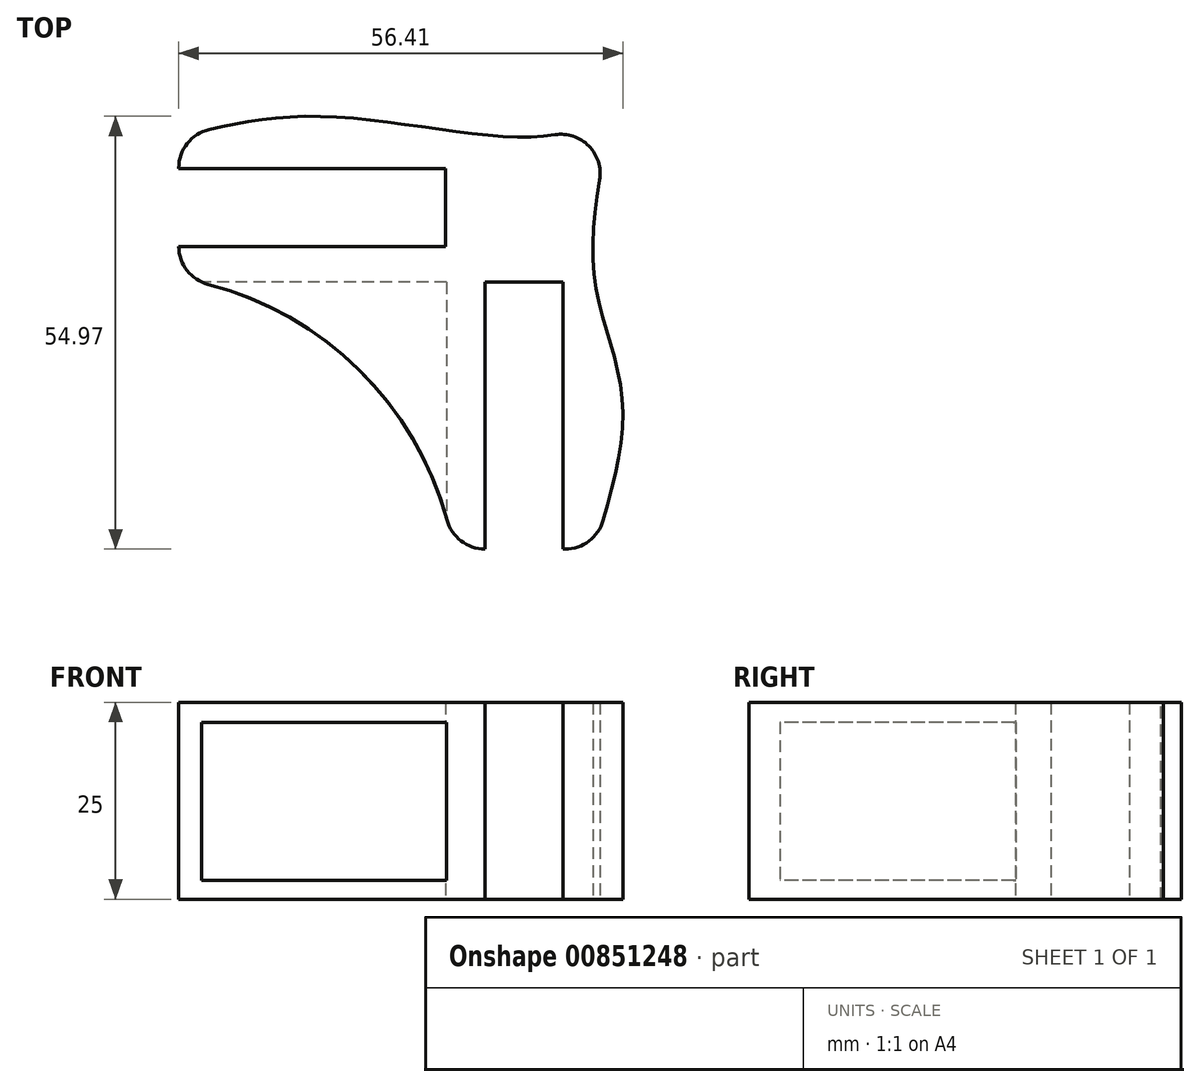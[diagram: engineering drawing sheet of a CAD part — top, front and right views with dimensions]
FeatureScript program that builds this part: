
annotation { "Feature Type Name" : "Feature", "Feature Type Description" : "" }
export const myFeature = defineFeature(function(context is Context, id is Id, definition is map)
    precondition{}
    {
        {
            var Q0;
            Q0=qCreatedBy(makeId("Top.planeOp"),FACE);
            var sketch = newSketch(context, id + "F0", { "sketchPlane" : qUnion([Q0])});
            skLineSegment(sketch, "E0.bottom", {"start": v(46.13, 46.63) * mm, "end": v(-43.87, 46.63) * mm, "construction": true});
            skLineSegment(sketch, "E0.top", {"start": v(46.13, -43.37) * mm, "end": v(-43.87, -43.37) * mm, "construction": true});
            skLineSegment(sketch, "E0.left", {"start": v(46.13, 46.63) * mm, "end": v(46.13, -43.37) * mm, "construction": true});
            skLineSegment(sketch, "E1", {"start": v(4.96, -9.48) * mm, "end": v(4.96, -43.37) * mm});
            skLineSegment(sketch, "E2", {"start": v(-4.96, -9.48) * mm, "end": v(-4.96, -43.37) * mm});
            skLineSegment(sketch, "E3", {"start": v(-10, 4.96) * mm, "end": v(-43.87, 4.96) * mm});
            skLineSegment(sketch, "E4", {"start": v(-10, -4.96) * mm, "end": v(-43.87, -4.96) * mm});
            skLineSegment(sketch, "E5", {"start": v(-10, -4.96) * mm, "end": v(-10, 4.96) * mm});
            skLineSegment(sketch, "E6", {"start": v(-4.96, -9.48) * mm, "end": v(4.96, -9.48) * mm});
            skLineSegment(sketch, "E7", {"start": v(-43.87, -4.96) * mm, "end": v(-43.87, -8.96) * mm});
            skLineSegment(sketch, "E8", {"start": v(-4.96, -43.37) * mm, "end": v(-4.97, -43.37) * mm});
            skLineSegment(sketch, "E9", {"start": v(-43.87, 4.96) * mm, "end": v(-43.87, 8.96) * mm});
            skLineSegment(sketch, "E10", {"start": v(4.96, -43.37) * mm, "end": v(8.96, -43.37) * mm});
            skFitSpline(sketch, "E11", {"points": [v(-43.87, 8.96) * mm, v(-25.72, 11.58) * mm, v(0, 8.96) * mm, v(11.1, 11.21) * mm], "startDerivative": vector(49.68, 12.5) * mm, "endDerivative": vector(36.5, 12.65) * mm});
            skFitSpline(sketch, "E12", {"points": [v(8.96, -43.37) * mm, v(12.48, -24.43) * mm, v(8.96, -8.93) * mm, v(11.1, 11.21) * mm], "startDerivative": vector(17.47, 57.6) * mm, "endDerivative": vector(12.47, 60.14) * mm});
            skArc(sketch, "E13", {"start": v(-9.8, -39.69) * mm, "mid": v(-22.32, -19.33) * mm, "end": v(-43.87, -8.96) * mm});
            skLineSegment(sketch, "E14.bottom", {"start": v(24.76, 22.31) * mm, "end": v(24.23, 22.31) * mm});
            skLineSegment(sketch, "E14.top", {"start": v(24.76, -47.4) * mm, "end": v(24.23, -47.4) * mm});
            skPoint(sketch, "E15.visualSharp", {"position": v(-8.96, -43.37) * mm});
            skArc(sketch, "E15.filletArc", {"start": v(-9.8, -39.69) * mm, "mid": v(-8, -42.35) * mm, "end": v(-4.97, -43.37) * mm});
            skSolve(sketch);
        }
        {
            var Q0;
            Q0 = qSketchRegion(id + "F0", true);
            extrude(context, id + "F1", {"entities" : qUnion([Q0]), "depth" : 25 * mm, "offsetDistance" : 25 * mm});
        }
        {
            var Q0;
            Q0=makeQuery(id+"F1.opExtrude","SWEPT_FACE",FACE,{"disambiguationData":[OSD([sQuery(id+"F0.wireOp",EDGE,"E7")])]});
            var sketch = newSketch(context, id + "F2", { "sketchPlane" : qUnion([Q0])});
            skLineSegment(sketch, "E16.bottom", {"start": v(9.46, 22.5) * mm, "end": v(39.68, 22.5) * mm});
            skLineSegment(sketch, "E16.top", {"start": v(9.46, 2.43) * mm, "end": v(39.68, 2.43) * mm});
            skLineSegment(sketch, "E16.left", {"start": v(9.46, 22.5) * mm, "end": v(9.46, 2.43) * mm});
            skLineSegment(sketch, "E16.right", {"start": v(39.68, 22.5) * mm, "end": v(39.68, 2.43) * mm});
            skSolve(sketch);
        }
        {
            var Q0;
            Q0=makeQuery(id+"F2.imprint","IMPRINT",FACE,{"disambiguationData":[TD([[makeQuery(id+"F2.imprint","IMPRINT",EDGE,{"derivedFrom":sQuery(id+"F2.wireOp",EDGE,"E16.bottom")}),-1.0]])]});
            extrude(context, id + "F3", {"entities" : qUnion([Q0]), "operationType" : NewBodyOperationType.REMOVE, "oppositeDirection" : true, "depth" : 34 * mm, "offsetDistance" : 25 * mm});
        }
        {
            var Q0;
            Q0=makeQuery(id+"F1.opExtrude","SWEPT_EDGE",EDGE,{"disambiguationData":[OSD([sQuery(id+"F0.wireOp",EDGE,"E7"),sQuery(id+"F0.wireOp",EDGE,"E13")])]});
            fillet(context, id + "F4", {"entities" : qUnion([Q0]), "radius" : 5 * mm, "tangentPropagation" : true, "allowEdgeOverflow" : false});
        }
        {
            var Q0;
            Q0=makeQuery(id+"F1.opExtrude","SWEPT_EDGE",EDGE,{"disambiguationData":[OSD([sQuery(id+"F0.wireOp",EDGE,"E10"),sQuery(id+"F0.wireOp",EDGE,"E12")])]});
            var Q1;
            Q1=makeQuery(id+"F1.opExtrude","SWEPT_EDGE",EDGE,{"disambiguationData":[OSD([sQuery(id+"F0.wireOp",EDGE,"E11"),sQuery(id+"F0.wireOp",EDGE,"E12")])]});
            var Q2;
            Q2=makeQuery(id+"F1.opExtrude","SWEPT_EDGE",EDGE,{"disambiguationData":[OSD([sQuery(id+"F0.wireOp",EDGE,"E9"),sQuery(id+"F0.wireOp",EDGE,"E11")])]});
            fillet(context, id + "F5", {"entities" : qUnion([Q0, Q1, Q2]), "radius" : 5 * mm, "tangentPropagation" : true, "allowEdgeOverflow" : false});
        }
    });
